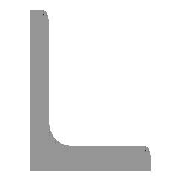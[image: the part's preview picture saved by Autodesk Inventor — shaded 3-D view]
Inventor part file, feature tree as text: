
AUTODESK INVENTOR PART (.ipt)
format: ipt  version: 2013 (Build 170138000, 138)  size: 130,048 bytes
history: native  units: mm (DEFAULTED — no unit token found)
features: other x4, plane x3, split x2, sketch x2
ambient origin geometry x8: Origin, YZ Plane, XZ Plane, XY Plane, X Axis, Y Axis, Z Axis, Center Point
bodies: Solid1 (feature_tree), Body (feature_tree)
feature tree (11):
  parser-record x1  (decoder bookkeeping rows leaked as tree rows — omitted from the tree; the rows remain in map.json)
  other  "Driven Length"
  other  "Start plane"
  other  "End plane"
  plane  "Work Plane4"
  split  "Split1"
  plane  "Work Plane5"
  split  "Split2"
  sketch  "Sketch3"  dims[d0=38.1mm]
  plane  "Work Plane3"
  sketch  "Sketch4"  dims[d1=38.1mm d2=4.7625mm d3=4.7625mm d4=1054.1mm d5=0.0mm d10=0.0mm d11=0.0mm d12=-0.0mm d13=1054.1mm d14=4.826mm d15=2.286mm d16=90.0deg d17=1054.1mm]
